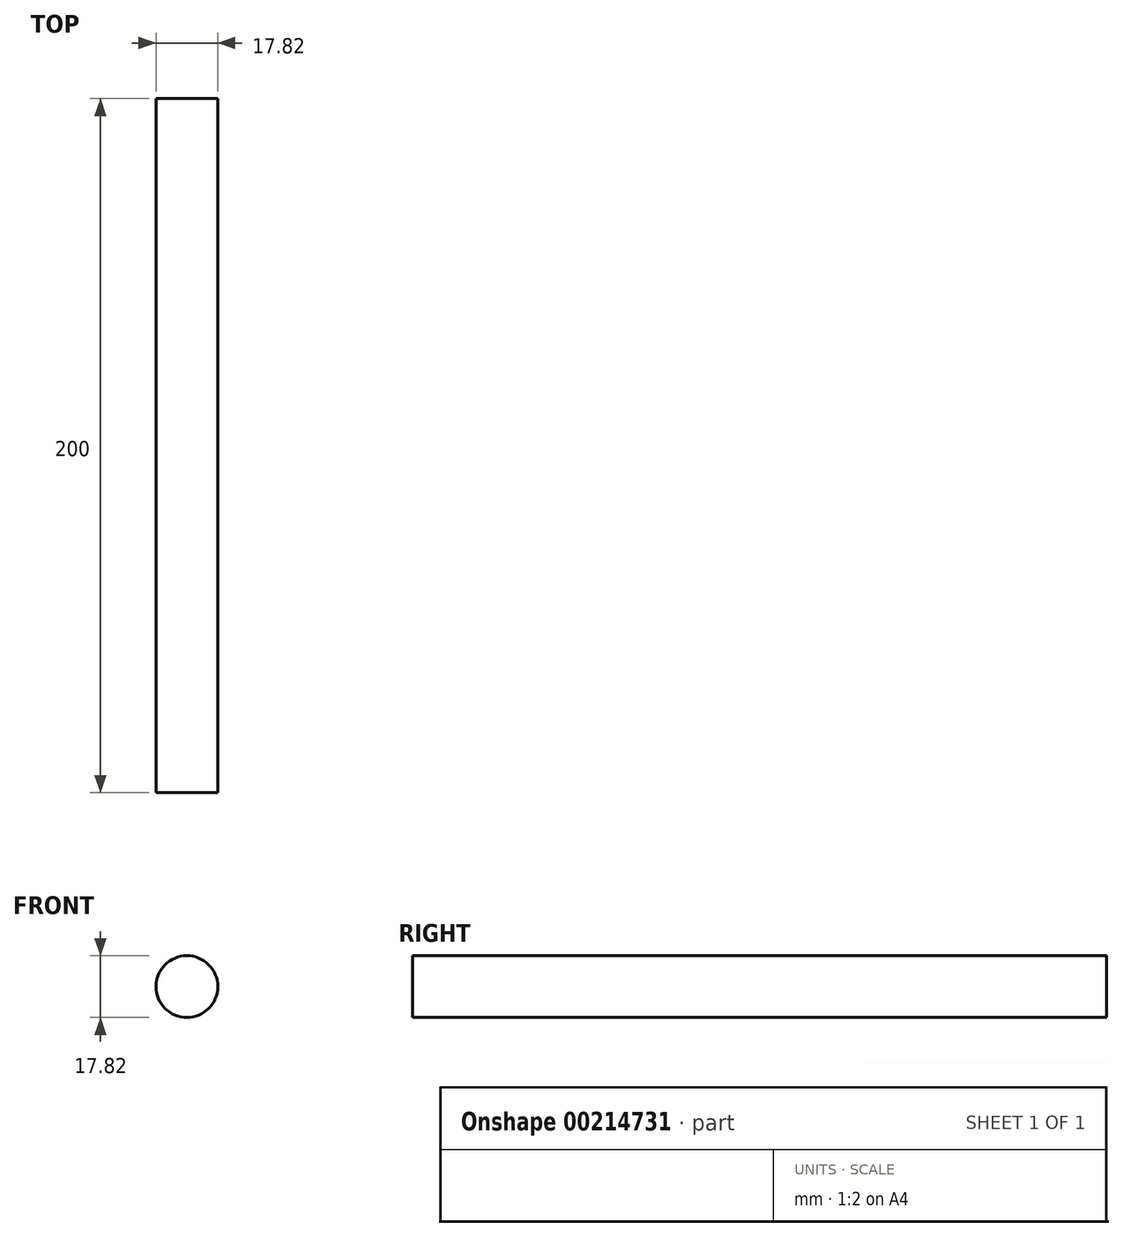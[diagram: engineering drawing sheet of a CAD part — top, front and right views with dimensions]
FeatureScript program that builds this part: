
annotation { "Feature Type Name" : "Feature", "Feature Type Description" : "" }
export const myFeature = defineFeature(function(context is Context, id is Id, definition is map)
    precondition{}
    {
        {
            var Q0;
            Q0=qCreatedBy(makeId("Front.planeOp"),FACE);
            var sketch = newSketch(context, id + "F0", { "sketchPlane" : qUnion([Q0])});
            skCircle(sketch, "E0", {"center": v(0, 0) * mm, "radius": 8.9 * mm});
            skSolve(sketch);
        }
        {
            var Q0;
            Q0=makeQuery(id+"F0.imprint","IMPRINT",FACE,{"disambiguationData":[TD([[makeQuery(id+"F0.imprint","IMPRINT",EDGE,{"derivedFrom":sQuery(id+"F0.wireOp",EDGE,"E0")}),1.0]])]});
            extrude(context, id + "F1", {"entities" : qUnion([Q0]), "depth" : 200 * mm});
        }
    });
